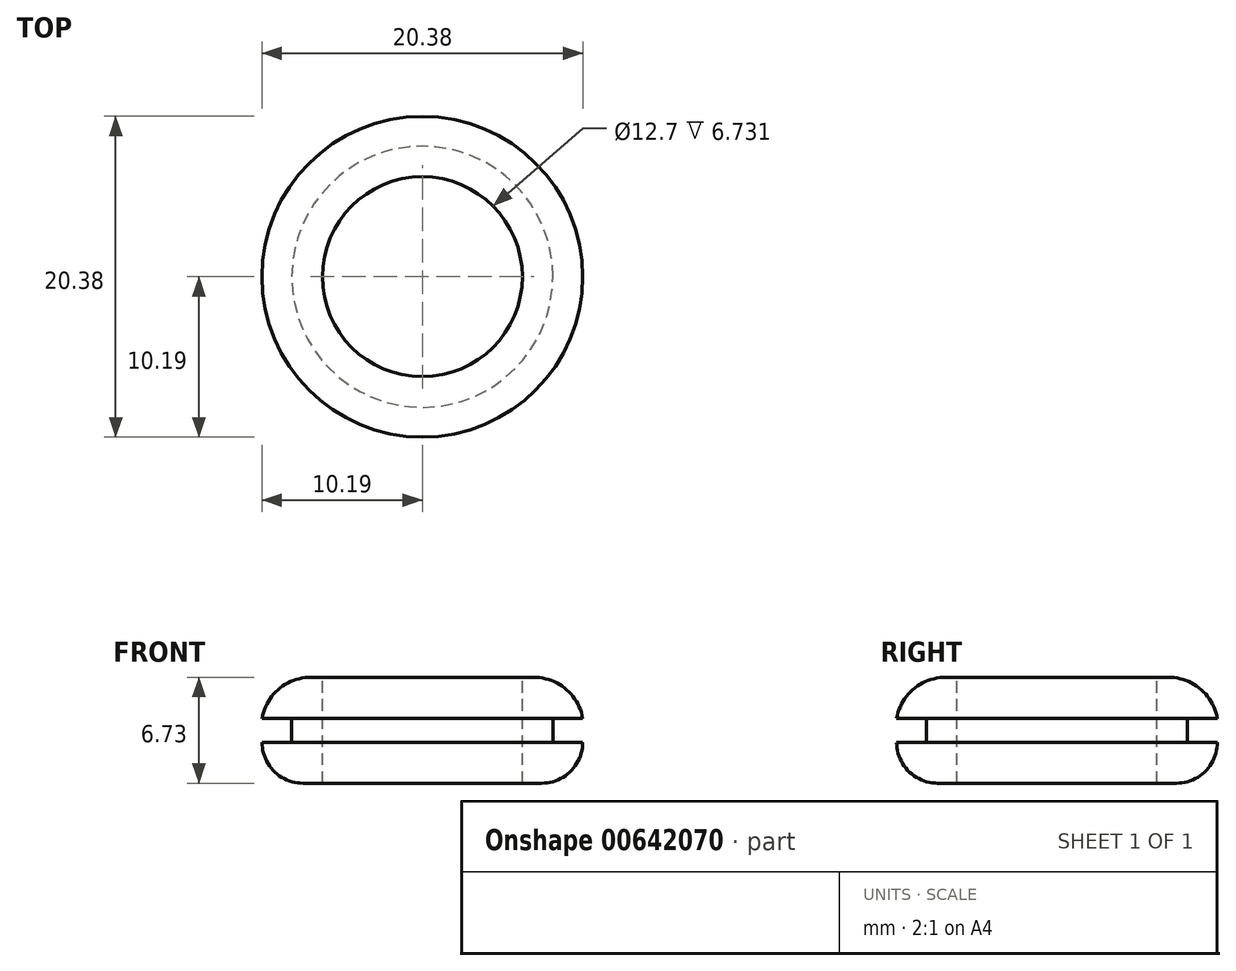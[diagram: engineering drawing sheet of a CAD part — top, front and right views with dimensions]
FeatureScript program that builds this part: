
annotation { "Feature Type Name" : "Feature", "Feature Type Description" : "" }
export const myFeature = defineFeature(function(context is Context, id is Id, definition is map)
    precondition{}
    {
        {
            var Q0;
            Q0=qCreatedBy(makeId("Front.planeOp"),FACE);
            var sketch = newSketch(context, id + "F0", { "sketchPlane" : qUnion([Q0])});
            skLineSegment(sketch, "E0", {"start": v(0, 0) * mm, "end": v(0, 6.73) * mm});
            skLineSegment(sketch, "E1", {"start": v(0, 6.73) * mm, "end": v(-7.06, 6.73) * mm});
            skLineSegment(sketch, "E2", {"start": v(0, 0) * mm, "end": v(0, 0) * mm});
            skLineSegment(sketch, "E3", {"start": v(0, 0) * mm, "end": v(-7.58, 0) * mm});
            skLineSegment(sketch, "E4.bottom", {"start": v(-10.19, 4.13) * mm, "end": v(-8.3, 4.13) * mm});
            skLineSegment(sketch, "E4.top", {"start": v(-10.19, 2.6) * mm, "end": v(-8.3, 2.6) * mm});
            skLineSegment(sketch, "E4.right", {"start": v(-8.3, 4.13) * mm, "end": v(-8.3, 2.6) * mm});
            skLineSegment(sketch, "E5", {"start": v(0, 3.37) * mm, "end": v(-10.19, 3.37) * mm, "construction": true});
            skArc(sketch, "E6.filletArc", {"start": v(-7.06, 6.73) * mm, "mid": v(-9.1, 6) * mm, "end": v(-10.19, 4.13) * mm});
            skArc(sketch, "E7.filletArc", {"start": v(-10.19, 2.6) * mm, "mid": v(-9.42, 0.76) * mm, "end": v(-7.58, 0) * mm});
            skLineSegment(sketch, "E8", {"start": v(-10.19, 2.6) * mm, "end": v(-10.19, 4.13) * mm, "construction": true});
            skSolve(sketch);
        }
        {
            var Q0;
            Q0 = qSketchRegion(id + "F0", true);
            var Q1;
            Q1=sQuery(id+"F0.wireOp",EDGE,"E0");
            revolve(context, id + "F1", {"entities" : qUnion([Q0]), "axis" : qUnion([Q1]), "revolveType" : RevolveType.FULL});
        }
        {
            var Q0;
            Q0=makeQuery(id+"F1.opRevolve","SWEPT_FACE",FACE,{"disambiguationData":[OSD([sQuery(id+"F0.wireOp",EDGE,"E1")])]});
            var sketch = newSketch(context, id + "F2", { "sketchPlane" : qUnion([Q0])});
            skCircle(sketch, "E9", {"center": v(0, 0) * mm, "radius": 6.35 * mm});
            skSolve(sketch);
        }
        {
            var Q0;
            Q0 = qSketchRegion(id + "F2", true);
            extrude(context, id + "F3", {"entities" : qUnion([Q0]), "operationType" : NewBodyOperationType.REMOVE, "endBound" : BoundingType.THROUGH_ALL, "oppositeDirection" : true, "depth" : 25.4 * mm, "offsetDistance" : 25.4 * mm});
        }
    });
